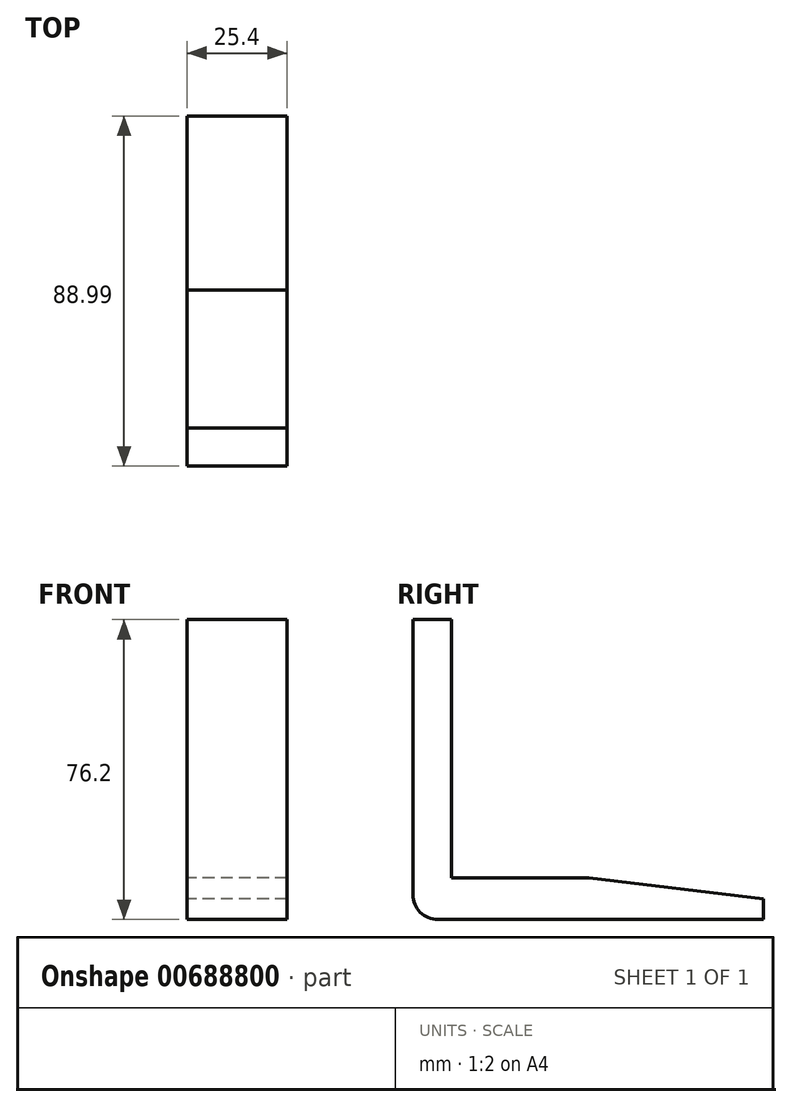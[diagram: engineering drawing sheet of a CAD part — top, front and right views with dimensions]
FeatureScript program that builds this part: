
annotation { "Feature Type Name" : "Feature", "Feature Type Description" : "" }
export const myFeature = defineFeature(function(context is Context, id is Id, definition is map)
    precondition{}
    {
        {
            var Q0;
            Q0=qCreatedBy(makeId("Right.planeOp"),FACE);
            var sketch = newSketch(context, id + "F0", { "sketchPlane" : qUnion([Q0])});
            skLineSegment(sketch, "E0", {"start": v(0, 0) * mm, "end": v(0, -69.85) * mm});
            skLineSegment(sketch, "E1", {"start": v(6.35, -76.2) * mm, "end": v(88.99, -76.2) * mm});
            skLineSegment(sketch, "E2", {"start": v(88.99, -76.2) * mm, "end": v(88.99, -70.9) * mm});
            skLineSegment(sketch, "E3", {"start": v(44.77, -65.6) * mm, "end": v(9.74, -65.6) * mm});
            skLineSegment(sketch, "E4", {"start": v(9.74, -65.6) * mm, "end": v(9.74, 0) * mm});
            skLineSegment(sketch, "E5", {"start": v(9.74, 0) * mm, "end": v(0, 0) * mm});
            skPoint(sketch, "E6.visualSharp", {"position": v(0, -76.2) * mm});
            skArc(sketch, "E6.filletArc", {"start": v(0, -69.85) * mm, "mid": v(1.86, -74.34) * mm, "end": v(6.35, -76.2) * mm});
            skLineSegment(sketch, "E7", {"start": v(44.77, -65.6) * mm, "end": v(88.99, -70.9) * mm});
            skPoint(sketch, "E8.orphan", {"position": v(88.99, -65.6) * mm});
            skSolve(sketch);
        }
        {
            var Q0;
            Q0 = qSketchRegion(id + "F0", true);
            extrude(context, id + "F1", {"entities" : qUnion([Q0]), "depth" : 25.4 * mm, "offsetDistance" : 25.4 * mm});
        }
    });
